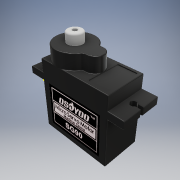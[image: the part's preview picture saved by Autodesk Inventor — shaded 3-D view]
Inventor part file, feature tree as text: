
AUTODESK INVENTOR PART (.ipt)
format: ipt  version: 2017 (Build 210142000, 142)  size: 1,671,680 bytes
history: native  units: mm
features: sketch x13, fillet x13, extrude x10, other x4, plane x1, projected_geometry x1
ambient origin geometry x8: Origin, YZ Plane, XZ Plane, XY Plane, X Axis, Y Axis, Z Axis, Center Point
bodies: Solid1 (feature_tree), Solid2 (feature_tree), Solid3 (feature_tree), Solid4 (feature_tree), Solid5 (feature_tree)
feature tree (42):
  extrude  "Extrusion1"  Depth=12.3mm
  plane  "Work Plane1"
  sketch  "Sketch2"  dims[d2=22.1mm d3=0.0mm d4=-6.6mm]
  extrude  "Extrusion2"  [1 undecoded]
  extrude  "Extrusion3"  Depth=2.4mm TaperAngle=0.0deg
  extrude  "Extrusion4"  Depth=2.0mm
  extrude  "Extrusion5"  Depth=1.0mm
  extrude  "Extrusion6"  Depth=2.4mm TaperAngle=0.0deg
  fillet  "Fillet1"  Radius=6.0mm
  extrude  "Extrusion7"  Depth=0.25mm TaperAngle=0.0deg
  fillet  "Fillet2"  Radius=4.5mm
  fillet  "Fillet3"  Radius=1.0mm
  fillet  "Fillet4"  Radius=4.8mm
  fillet  "Fillet5"  Radius=1.5mm
  fillet  "Fillet6"  Radius=3.0mm
  fillet  "Fillet7"  Radius=0.5mm
  fillet  "Fillet8"  Radius=0.25mm
  fillet  "Fillet9"  Radius=0.25mm
  fillet  "Fillet10"  Radius=0.25mm
  fillet  "Fillet11"  Radius=0.25mm
  fillet  "Fillet12"  Radius=0.25mm
  extrude  "Extrusion8"  Depth=0.25mm
  extrude  "Extrusion9"  Depth=0.25mm
  extrude  "Extrusion10"  Depth=3.0mm
  fillet  "Fillet13"  Radius=3.0mm
  other  "Decal1"
  other  "Decal2"
  sketch  "Sketch1"  dims[d0=22.6mm d1=12.3mm]
  sketch  "Sketch3"  dims[d5=32.0mm d6=2.4mm d7=0.0mm]
  sketch  "Sketch4"  dims[d8=2.0mm d9=2.0mm]
  sketch  "Sketch5"  dims[d10=1.0mm d11=1.0mm]
  projected_geometry  "Projected Loop1"
  sketch  "Sketch6"  dims[d12=2.4mm d13=0.0mm d14=4.5mm d15=0.0mm d16=6.0mm]
  sketch  "Sketch7"  dims[d17=10.3mm d18=0.3mm d19=0.0mm d20=4.5mm d21=0.0mm d22=1.0mm d23=4.8mm d24=1.5mm d25=3.0mm d26=0.0mm d27=0.5mm d28=0.25mm d29=0.25mm d30=0.25mm d31=0.25mm d32=0.25mm]
  sketch  "Sketch8"  dims[d33=0.25mm d34=0.25mm]
  sketch  "Sketch9"  dims[d35=0.25mm d36=0.25mm]
  sketch  "Sketch10"  dims[d37=0.25mm d38=1.0mm d39=3.0mm d40=0.0mm]
  sketch  "Sketch11"  dims[d41=1.0mm]
  sketch  "Sketch12"  dims[d42=3.0mm d43=0.0mm]
  other  "Image1"
  sketch  "Sketch13"  dims[d44=1.0mm d45=3.0mm d46=0.0mm d47=0.25mm]
  other  "Image2"
note: 1 required parameter value undecoded (feature->parameter linkage not recoverable at this tier; creation-order binding heuristic only, values carry confidence <= 0.55)
